# Revit family: IEK_Выключатель_ОУ_10А_1кл_IP54_ГЕРМЕС_PLUS
name_source: partatom
category: Выключатели
units: mm (PartAtom-declared; Revit-internal decimal feet)

## family parameters
Всегда вертикально = Да
На основе рабочей плоскости = Нет
Общий = Нет
При загрузке вырезать с полостями = Нет
Размер круглого соединителя = Использовать диаметр
Сохранять ориентацию аннотаций = Да
Тип детали = Переключатель
Точка расчета площади = Нет

## types (3) — shared parameters
ADSK_URL страницы изделия = https://qr.iek.group
ADSK_Версия Revit = v2019
ADSK_Версия семейства = 01.10.25
ADSK_Группирование = Электроустановочные изделия низковольтные
ADSK_Единица измерения = шт.
ADSK_Завод-изготовитель = IEK
ADSK_Количество фаз = 1
ADSK_Количество фаз числовое = 1
ADSK_Марка = ГЕРМЕС PLUS
ADSK_Масса = 0.095
ADSK_Материал = Цвет белый
ADSK_Материал наименование = Пластик
ADSK_Напряжение = 220 В
URL = https://www.iek.ru
Высота = 72 мм
Глубина = 52 мм
Изготовитель = IEK
Описание = Изделия серии "ГЕРМЕС PLUS" используются в помещениях с повышенной влажностью или запыленностью, а также под навесом на открытом воздухе.
Степень защиты = IP54
Тип монтажа = Поверхность монтажа (открытая установка)
Ширина = 72 мм

## per-type parameters (varying)
| type | ADSK_Код изделия | ADSK_Наименование | ADSK_Наименование краткое |
| ВС20-1-0-ГПБ | EVMP10-K01-10-54-EC | Выключатель 1-клавишный для открытой установки ВС20-1-0-ГПБ IP54 ГЕРМЕС PLUS (цвет клавиши: белый) IEK | ВС20-1-0-ГПБ |
| ВСп20-1-0-ГПБ_Проходной | EVMP12-K01-10-54-EC | Выключатель 1-клавишный для открытой установки проходной ВСп20-1-0-ГПБ IP54 ГЕРМЕС PLUS (цвет клавиши: белый) IEK | ВСп20-1-0-ГПБ |
| ВСк20-1-0-ГПБ_Кнопочный | EVMP13-K01-10-54-EC | Выключатель 1-клавишный для открытой установки кнопочный ВСк20-1-0-ГПБ IP54 ГЕРМЕС PLUS (цвет клавиши: белый) IEK | ВСк20-1-0-ГПБ |
